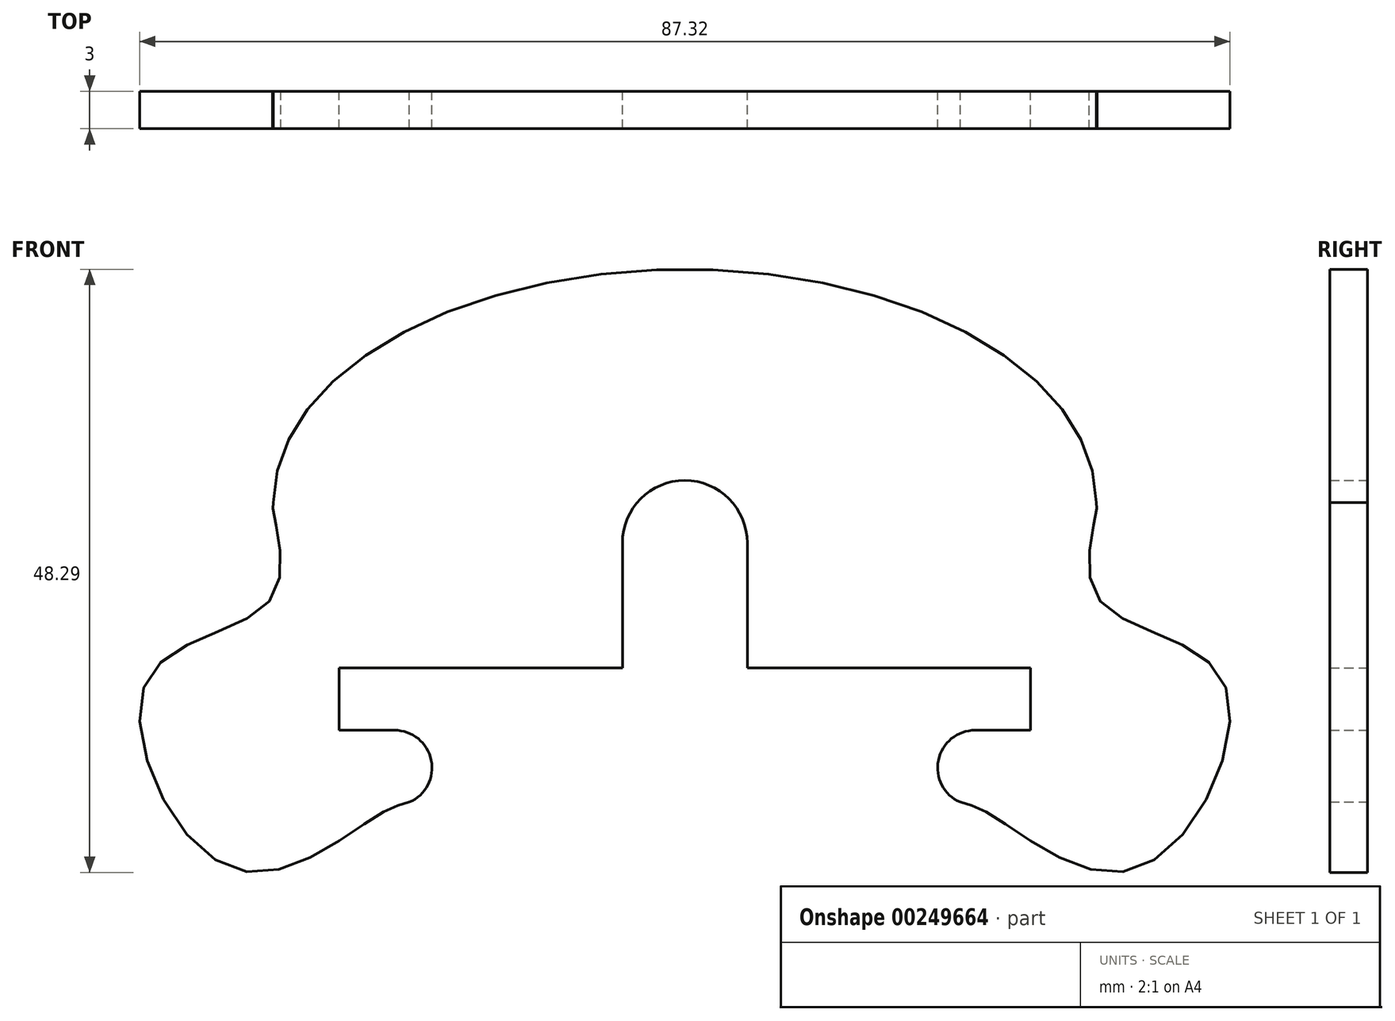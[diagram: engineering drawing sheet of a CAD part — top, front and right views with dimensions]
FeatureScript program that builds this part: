
annotation { "Feature Type Name" : "Feature", "Feature Type Description" : "" }
export const myFeature = defineFeature(function(context is Context, id is Id, definition is map)
    precondition{}
    {
        {
            var Q0;
            Q0=qCreatedBy(makeId("Front.planeOp"),FACE);
            var sketch = newSketch(context, id + "F0", { "sketchPlane" : qUnion([Q0])});
            skLineSegment(sketch, "E0", {"start": v(-27.68, -14.35) * mm, "end": v(-27.68, -9.35) * mm});
            skLineSegment(sketch, "E1", {"start": v(-27.68, -9.35) * mm, "end": v(-5, -9.35) * mm});
            skLineSegment(sketch, "E2", {"start": v(5, -9.35) * mm, "end": v(27.68, -9.35) * mm});
            skLineSegment(sketch, "E3", {"start": v(27.68, -14.35) * mm, "end": v(27.68, -9.35) * mm});
            skLineSegment(sketch, "E4", {"start": v(5, -9.35) * mm, "end": v(5, 0.65) * mm});
            skLineSegment(sketch, "E5", {"start": v(-5, -9.35) * mm, "end": v(-5, 0.65) * mm});
            skArc(sketch, "E6", {"start": v(5, 0.65) * mm, "mid": v(0, 5.65) * mm, "end": v(-5, 0.65) * mm});
            skLineSegment(sketch, "E7", {"start": v(27.68, -14.35) * mm, "end": v(23.25, -14.35) * mm});
            skFitSpline(sketch, "E8", {"points": [v(32.95, 3.9) * mm, v(33, 3.4) * mm, v(33.02, -3.69) * mm, v(43.1, -10.37) * mm, v(36.2, -25.42) * mm, v(24.8, -21.29) * mm, v(22.06, -20.1) * mm]});
            skArc(sketch, "E9", {"start": v(23.25, -14.35) * mm, "mid": v(20.3, -16.74) * mm, "end": v(22.06, -20.1) * mm});
            skLineSegment(sketch, "E10", {"start": v(-27.68, -14.35) * mm, "end": v(-23.25, -14.35) * mm});
            skFitSpline(sketch, "E11", {"points": [v(-32.95, 3.9) * mm, v(-33, 3.4) * mm, v(-33.02, -3.69) * mm, v(-43.1, -10.37) * mm, v(-36.2, -25.42) * mm, v(-24.8, -21.29) * mm, v(-22.06, -20.1) * mm]});
            skArc(sketch, "E12", {"start": v(-22.06, -20.1) * mm, "mid": v(-20.3, -16.74) * mm, "end": v(-23.25, -14.35) * mm});
            skEllipticalArc(sketch, "E13", {});
            const initialGuessF0  = {"E13": [0, 0.0038925380000000586, 32.949969, 0, 0.032949969, 0.018668385000000003, 0, 3.141593]};
            skSetInitialGuess(sketch, initialGuessF0);
            skSolve(sketch);
        }
        {
            var Q0;
            Q0=makeQuery(id+"F0.imprint","IMPRINT",FACE,{"disambiguationData":[TD([[makeQuery(id+"F0.imprint","IMPRINT",EDGE,{"derivedFrom":sQuery(id+"F0.wireOp",EDGE,"E0")}),1.0]])]});
            extrude(context, id + "F1", {"entities" : qUnion([Q0]), "depth" : 3 * mm});
        }
    });
